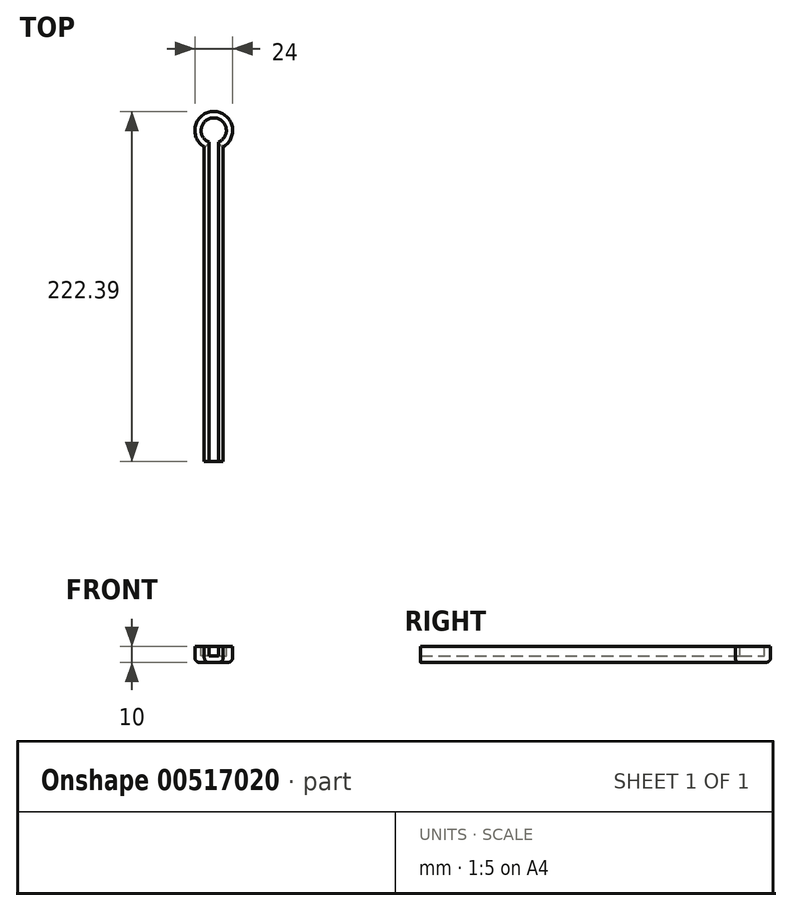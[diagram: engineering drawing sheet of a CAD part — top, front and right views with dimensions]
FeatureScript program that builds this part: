
annotation { "Feature Type Name" : "Feature", "Feature Type Description" : "" }
export const myFeature = defineFeature(function(context is Context, id is Id, definition is map)
    precondition{}
    {
        {
            var Q0;
            Q0=qCreatedBy(makeId("Top.planeOp"),FACE);
            var sketch = newSketch(context, id + "F0", { "sketchPlane" : qUnion([Q0])});
            skLineSegment(sketch, "E0.bottom", {"start": v(-6, 100) * mm, "end": v(6, 100) * mm});
            skLineSegment(sketch, "E0.top", {"start": v(-6, -100) * mm, "end": v(6, -100) * mm});
            skLineSegment(sketch, "E0.left", {"start": v(-6, 100) * mm, "end": v(-6, -100) * mm});
            skLineSegment(sketch, "E0.right", {"start": v(6, 100) * mm, "end": v(6, -100) * mm});
            skCircle(sketch, "E1", {"center": v(0, 110.4) * mm, "radius": 12 * mm});
            skSolve(sketch);
        }
        {
            var Q0;
            Q0 = qSketchRegion(id + "F0", true);
            extrude(context, id + "F1", {"entities" : qUnion([Q0]), "depth" : 10 * mm, "offsetDistance" : 25 * mm});
        }
        {
            var Q0;
            Q0=makeQuery(id+"F1.opExtrude","CAP_FACE",FACE,{"disambiguationData":[OSD([sQuery(id+"F0.wireOp",EDGE,"E0.top"),sQuery(id+"F0.wireOp",EDGE,"E0.left"),sQuery(id+"F0.wireOp",EDGE,"E0.right"),sQuery(id+"F0.wireOp",EDGE,"E1")])],"isStart":false});
            var sketch = newSketch(context, id + "F2", { "sketchPlane" : qUnion([Q0])});
            skArc(sketch, "E2", {"start": v(3, 102.98) * mm, "mid": v(0, 118.4) * mm, "end": v(-3, 102.98) * mm});
            skLineSegment(sketch, "E3", {"start": v(3, -100) * mm, "end": v(3, 102.98) * mm});
            skLineSegment(sketch, "E4", {"start": v(-3, -100) * mm, "end": v(-3, 102.98) * mm});
            skSolve(sketch);
        }
        {
            var Q0;
            Q0=makeQuery(id+"F2.imprint","IMPRINT",FACE,{"disambiguationData":[TD([[makeQuery(id+"F2.imprint","IMPRINT",EDGE,{"derivedFrom":sQuery(id+"F2.wireOp",EDGE,"E2")}),1.0]])]});
            extrude(context, id + "F3", {"entities" : qUnion([Q0]), "operationType" : NewBodyOperationType.REMOVE, "oppositeDirection" : true, "depth" : 6 * mm, "offsetDistance" : 25 * mm});
        }
        {
            var Q0;
            Q0=makeQuery(id+"F1.opExtrude","CAP_EDGE",EDGE,{"disambiguationData":[OSD([sQuery(id+"F0.wireOp",EDGE,"E0.right")])],"isStart":true});
            var Q1;
            Q1=makeQuery(id+"F1.opExtrude","CAP_EDGE",EDGE,{"disambiguationData":[OSD([sQuery(id+"F0.wireOp",EDGE,"E1")])],"isStart":true});
            var Q2;
            Q2=makeQuery(id+"F1.opExtrude","CAP_EDGE",EDGE,{"disambiguationData":[OSD([sQuery(id+"F0.wireOp",EDGE,"E0.left")])],"isStart":true});
            fillet(context, id + "F4", {"entities" : qUnion([Q0, Q1, Q2]), "radius" : 3 * mm, "tangentPropagation" : true, "allowEdgeOverflow" : false});
        }
    });
